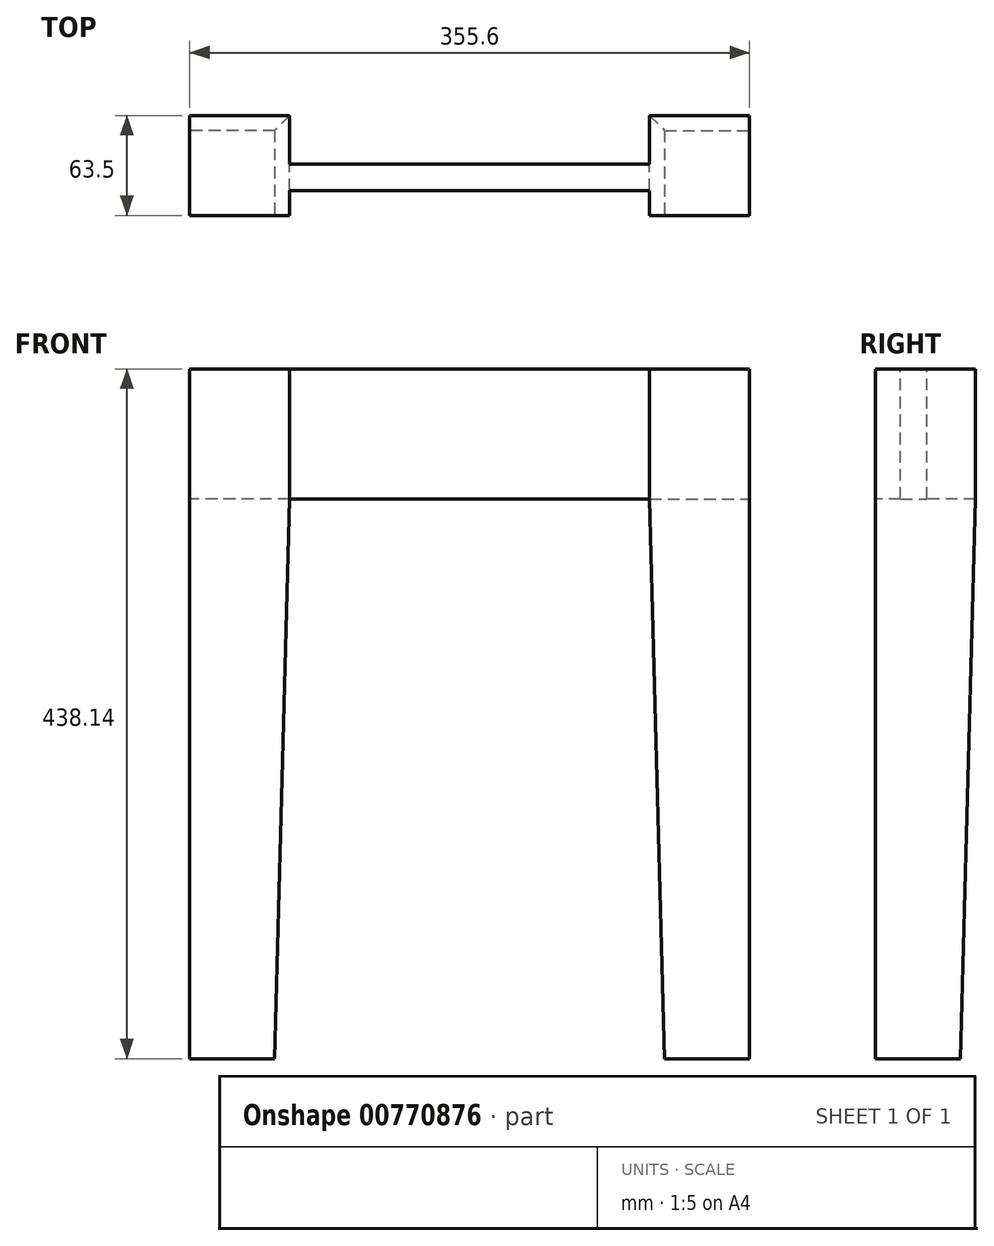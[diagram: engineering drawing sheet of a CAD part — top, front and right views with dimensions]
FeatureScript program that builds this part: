
annotation { "Feature Type Name" : "Feature", "Feature Type Description" : "" }
export const myFeature = defineFeature(function(context is Context, id is Id, definition is map)
    precondition{}
    {
        {
            var Q0;
            Q0=qCreatedBy(makeId("Front.planeOp"),FACE);
            var sketch = newSketch(context, id + "F0", { "sketchPlane" : qUnion([Q0])});
            skLineSegment(sketch, "E0.bottom", {"start": v(31.75, -219.08) * mm, "end": v(-31.75, -219.08) * mm});
            skLineSegment(sketch, "E0.top", {"start": v(31.75, 219.08) * mm, "end": v(-31.75, 219.08) * mm});
            skLineSegment(sketch, "E0.left", {"start": v(31.75, -219.08) * mm, "end": v(31.75, 219.08) * mm});
            skLineSegment(sketch, "E0.right", {"start": v(-31.75, -219.08) * mm, "end": v(-31.75, 219.08) * mm});
            skPoint(sketch, "E0.middle", {"position": v(0, 0) * mm});
            skLineSegment(sketch, "E1", {"start": v(31.75, 219.08) * mm, "end": v(31.75, 136.53) * mm});
            skLineSegment(sketch, "E2", {"start": v(-31.75, -219.08) * mm, "end": v(22.23, -219.08) * mm});
            skLineSegment(sketch, "E3", {"start": v(22.23, -219.08) * mm, "end": v(31.75, 136.53) * mm});
            skSolve(sketch);
        }
        {
            var Q0;
            {var subQ1=sQuery(id+"F0.wireOp",EDGE,"E0.top");Q0=makeQuery(id+"F0.imprint","IMPRINT",FACE,{"disambiguationData":[TD([[makeQuery(id+"F0.imprint","IMPRINT",EDGE,{"derivedFrom":subQ1}),1.0]])]});}
            extrude(context, id + "F1", {"entities" : qUnion([Q0]), "depth" : 63.5 * mm, "offsetDistance" : 25.4 * mm});
        }
        {
            var Q0;
            Q0=makeQuery(id+"F1.opExtrude","SWEPT_FACE",FACE,{"disambiguationData":[OSD([sQuery(id+"F0.wireOp",EDGE,"E0.right")])]});
            var sketch = newSketch(context, id + "F2", { "sketchPlane" : qUnion([Q0])});
            skLineSegment(sketch, "E4", {"start": v(0, 219.08) * mm, "end": v(0, 136.53) * mm});
            skLineSegment(sketch, "E5", {"start": v(63.5, -219.08) * mm, "end": v(9.52, -219.08) * mm});
            skLineSegment(sketch, "E6", {"start": v(0, 136.53) * mm, "end": v(9.52, -219.08) * mm});
            skSolve(sketch);
        }
        {
            var Q0;
            {var subQ0=sQuery(id+"F2.wireOp",EDGE,"E6");Q0=makeQuery(id+"F2.imprint","IMPRINT",FACE,{"disambiguationData":[TD([[makeQuery(id+"F2.imprint","IMPRINT",EDGE,{"derivedFrom":subQ0}),-1.0]])]});}
            extrude(context, id + "F3", {"entities" : qUnion([Q0]), "operationType" : NewBodyOperationType.REMOVE, "oppositeDirection" : true, "depth" : 63.5 * mm, "offsetDistance" : 25.4 * mm});
        }
        {
            var Q0;
            Q0=makeQuery(id+"F1.opExtrude","SWEPT_FACE",FACE,{"disambiguationData":[OSD([sQuery(id+"F0.wireOp",EDGE,"E0.top")])]});
            var sketch = newSketch(context, id + "F4", { "sketchPlane" : qUnion([Q0])});
            skLineSegment(sketch, "E7", {"start": v(31.75, -63.5) * mm, "end": v(31.75, -47.62) * mm});
            skLineSegment(sketch, "E8.bottom", {"start": v(31.75, -47.62) * mm, "end": v(260.35, -47.62) * mm});
            skLineSegment(sketch, "E8.top", {"start": v(31.75, -30.93) * mm, "end": v(260.35, -30.93) * mm});
            skLineSegment(sketch, "E8.left", {"start": v(31.75, -47.62) * mm, "end": v(31.75, -30.93) * mm});
            skLineSegment(sketch, "E8.right", {"start": v(260.35, -47.62) * mm, "end": v(260.35, -30.93) * mm});
            skSolve(sketch);
        }
        {
            var Q0;
            Q0=makeQuery(id+"F1.opExtrude","SWEPT_BODY",BODY,{"disambiguationData":[OSD([sQuery(id+"F0.wireOp",EDGE,"E0.bottom"),sQuery(id+"F0.wireOp",EDGE,"E0.top"),sQuery(id+"F0.wireOp",EDGE,"E0.left"),sQuery(id+"F0.wireOp",EDGE,"E0.right"),sQuery(id+"F0.wireOp",EDGE,"E3")])]});
            var Q1;
            Q1=qCreatedBy(makeId("Right.planeOp"),FACE);
            mirror(context, id + "F5", {"operationType" : NewBodyOperationType.ADD, "entities" : qUnion([Q0]), "mirrorPlane" : qUnion([Q1])});
        }
        {
            var Q0;
            Q0=makeQuery(id+"F4.imprint","IMPRINT",FACE,{"disambiguationData":[TD([[makeQuery(id+"F4.imprint","IMPRINT",EDGE,{"derivedFrom":sQuery(id+"F4.wireOp",EDGE,"E8.bottom")}),1.0]])]});
            extrude(context, id + "F6", {"entities" : qUnion([Q0]), "operationType" : NewBodyOperationType.ADD, "depth" : -82.55 * mm, "offsetDistance" : 25.4 * mm});
        }
        {
            var Q0;
            Q0=makeQuery(id+"F6.opExtrude","CAP_EDGE",EDGE,{"disambiguationData":[OSD([sQuery(id+"F4.wireOp",EDGE,"E8.bottom")])],"isStart":true});
            cPoint(context, id + "F7", {"entities" : qUnion([Q0]), "parameter" : 0.5});
        }
        {
            var Q0;
            Q0=makeQuery(id+"F6.opExtrude","CAP_EDGE",EDGE,{"disambiguationData":[OSD([sQuery(id+"F4.wireOp",EDGE,"E8.top")])],"isStart":true});
            cPoint(context, id + "F8", {"entities" : qUnion([Q0]), "parameter" : 0.5});
        }
        {
            var Q0;
            Q0=makeQuery(id+"F6.opExtrude","CAP_EDGE",EDGE,{"disambiguationData":[OSD([sQuery(id+"F4.wireOp",EDGE,"E8.bottom")])],"isStart":false});
            cPoint(context, id + "F9", {"entities" : qUnion([Q0]), "parameter" : 0.5});
        }
        {
            var Q0;
            Q0=qCreatedBy(id+"F7",VERTEX);
            var Q1;
            Q1=qCreatedBy(id+"F8",VERTEX);
            var Q2;
            Q2=qCreatedBy(id+"F9",VERTEX);
            cPlane(context, id + "F10", {"entities" : qUnion([Q0, Q1, Q2]), "cplaneType" : CPlaneType.THREE_POINT, "offset" : 25.4 * mm, "width" : 152.4 * mm, "height" : 152.4 * mm});
        }
        {
            var Q0;
            {var subQ0=makeQuery(id+"F1.opExtrude","CAP_FACE",FACE,{"disambiguationData":[OSD([sQuery(id+"F0.wireOp",EDGE,"E0.bottom"),sQuery(id+"F0.wireOp",EDGE,"E0.top"),sQuery(id+"F0.wireOp",EDGE,"E0.left"),sQuery(id+"F0.wireOp",EDGE,"E0.right"),sQuery(id+"F0.wireOp",EDGE,"E3")])],"isStart":false});Q0=makeQuery(id+"F5.boolean.opBoolean","MERGE",FACE,{"derivedFrom":[subQ0,makeQuery(id+"F5.opPattern","COPY",FACE,{"derivedFrom":subQ0,"instanceName":"1"})]});}
            var sketch = newSketch(context, id + "F11", { "sketchPlane" : qUnion([Q0])});
            skLineSegment(sketch, "E9", {"start": v(31.75, 219.08) * mm, "end": v(31.75, 136.53) * mm});
            skLineSegment(sketch, "E10", {"start": v(-31.75, -219.08) * mm, "end": v(22.23, -219.08) * mm});
            skLineSegment(sketch, "E11", {"start": v(22.23, -219.08) * mm, "end": v(31.75, 136.53) * mm});
            skSolve(sketch);
        }
        {
            var Q0;
            {var subQ0=sQuery(id+"F11.wireOp",EDGE,"E11");Q0=makeQuery(id+"F11.imprint","IMPRINT",FACE,{"disambiguationData":[TD([[makeQuery(id+"F11.imprint","IMPRINT",EDGE,{"derivedFrom":subQ0}),-1.0]])]});}
            extrude(context, id + "F12", {"entities" : qUnion([Q0]), "operationType" : NewBodyOperationType.REMOVE, "oppositeDirection" : true, "depth" : 63.5 * mm, "offsetDistance" : 25.4 * mm});
        }
        {
            var Q0;
            Q0=makeQuery(id+"F1.opExtrude","SWEPT_BODY",BODY,{"disambiguationData":[OSD([sQuery(id+"F0.wireOp",EDGE,"E0.bottom"),sQuery(id+"F0.wireOp",EDGE,"E0.top"),sQuery(id+"F0.wireOp",EDGE,"E0.left"),sQuery(id+"F0.wireOp",EDGE,"E0.right"),sQuery(id+"F0.wireOp",EDGE,"E3")])]});
            var Q1;
            Q1=qCreatedBy(id+"F10.planeOp",FACE);
            mirror(context, id + "F13", {"operationType" : NewBodyOperationType.ADD, "entities" : qUnion([Q0]), "mirrorPlane" : qUnion([Q1])});
        }
    });
